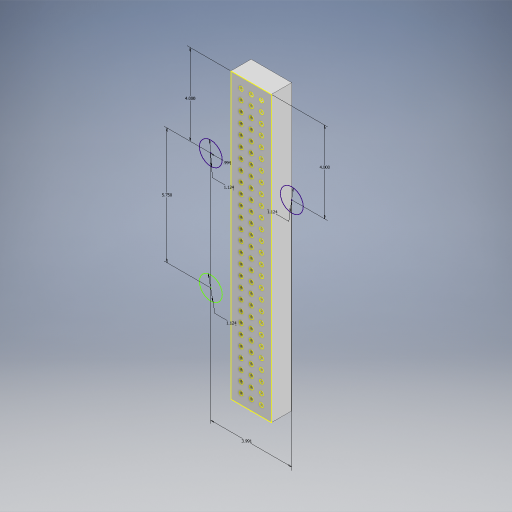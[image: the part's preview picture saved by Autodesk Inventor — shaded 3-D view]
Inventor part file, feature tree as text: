
AUTODESK INVENTOR PART (.ipt)
format: ipt  version: 2024.2 (Build 282272000, 272)  size: 437,760 bytes
history: native  units: in
note: dims shown in document units (in); Inventor stores cm internally (conversion verified against a paired STEP export)
features: sketch x3, extrude x2, projected_geometry x1
ambient origin geometry x8: Origin, YZ Plane, XZ Plane, XY Plane, X Axis, Y Axis, Z Axis, Center Point
bodies: Solid1 (feature_tree)
feature tree (6):
  extrude  "Extrusion1"  Depth=1.0in
  extrude  "Extrusion2"  Depth=14.0in
  sketch  "Sketch3"  dims[d5=0.5in d6=0.5in d7=1.1811in d9=0.5in d10=10.6299in d12=0.5in d15=14.0in d16=0.0in d17=1.124in d18=4.0in d19=1.124in d20=4.0in d21=3.991in d22=0.994in d23=1.124in d24=5.75in]
  sketch  "Sketch1"  dims[d0=2.0in d1=1.0in]
  sketch  "Sketch2"  dims[d2=14.0in d3=0.0in d4=0.196in]
  projected_geometry  "Projected Loop1"
